# Revit family: 210_eca9cc18b7f04a538e39d5ccf5370a
name_source: partatom
category: Mechanical Equipment
revit_build: Autodesk Revit 2018 (Build: 20170223_1515(x64)
units: mm (PartAtom-declared; Revit-internal decimal feet)

## family parameters
Always vertical = Yes
Cut with Voids When Loaded = No
Part Type = Breaks Into
Room Calculation Point = No
Round Connector Dimension = Use Diameter
Shared = No
Work Plane-Based = No

## types (1)
- UNI 3 RER (700040)
    CAT0 = Yes
    Clearance Zone Front Depth = 75 mm  [stored 0.246063 ft]
    DEXH = 160 mm
    DEXT = 160 mm
    DEXT9 = 125 mm
    DL = 48 mm  [stored 0.15748 ft]
    DL__ve = -48 mm  [stored -0.15748 ft]
    DOUT = 160 mm
    DSUP = 160 mm
    Description = UNI 3 RER (700040)
    EXHX = 244 mm  [stored 0.800525 ft]
    EXHY = 120 mm  [stored 0.393701 ft]
    EXT9X = 0 mm  [stored 0 ft]
    EXT9Y = 190 mm  [stored 0.62336 ft]
    EXTX = 244 mm  [stored 0.800525 ft]
    EXTY = 120 mm  [stored 0.393701 ft]
    H = 700 mm  [stored 2.29659 ft]
    H2 = 350 mm  [stored 1.14829 ft]
    L2 = 360 mm  [stored 1.1811 ft]
    MC Product Code = UNI 3 RER (700040)
    Manufacturer = Flexit
    OUTX = 244 mm  [stored 0.800525 ft]
    OUTY = 360 mm  [stored 1.1811 ft]
    QmdConnectorList = 221;DSUP;231;DOUT;232;DOUT;241;DEXT;243;DEXT;249;DEXT9;251;DEXH
    REXH = 80 mm  [stored 0.262467 ft]
    REXT = 80 mm  [stored 0.262467 ft]
    REXT9 = 63 mm
    ROUT = 80 mm  [stored 0.262467 ft]
    RSUP = 80 mm  [stored 0.262467 ft]
    SUPX = 244 mm  [stored 0.800525 ft]
    SUPY = 360 mm  [stored 1.1811 ft]
    W = 520 mm  [stored 1.70604 ft]
    magiPartTypeId = 210
    magiProductFamilyId = eca9cc18b7f04a538e39d5ccf5370a
    magiProductId = eca9cc18b7f04a538e39d5ccf5370a

note: [stored X ft] marks values corroborated as IEEE doubles in the binary element streams (Revit-internal decimal feet)

## geometry (parser evidence)
native form markers: Sweep x2
no freeform markers — native parametric forms only
